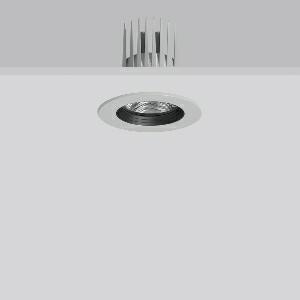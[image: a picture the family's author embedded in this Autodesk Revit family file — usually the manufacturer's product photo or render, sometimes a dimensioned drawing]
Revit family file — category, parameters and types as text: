
# Revit family: heledon_mini_e_901748_004_2_1676
name_source: partatom
category: Lighting Fixtures
units: mm (PartAtom-declared; Revit-internal decimal feet)

## family parameters
Cut with Voids When Loaded = No
Host = Face
Light Source = No
Part Type = Normal
Room Calculation Point = No
Round Connector Dimension = Use Diameter
Shared = No

## types (1)
- HELEDON mini E (1 x LED Modul 927, 3400 lm, 2700)
    Apparent Load = 29 VA
    Approval mark = CE
    CIE Flux Codes = 100 100 100 100 100
    Color Rendering = 92
    Color Temperature = 2700
    Default Elevation = 1800 mm
    Description = Series: HELEDON mini
Round recessed downlight. Housing: die-cast aluminium, powder-coated. Black plastic ring and recessed LED to prevent glare from the side. Optical assembly with reflector made of MIRO-Silver with 98% total light reflection for outstanding efficiency - can be changed without tools. Best colour rendering index Ra>90. Suitable for Recessed ceiling mounting. Installation without tools thanks to spring fastening system. Including separate LED converter with connecting cable 600 mm.High quality converter without flickering and stroboscopic effect. Through-wiring box (5 pole) available as accessory. The following accessories can be mounted without use of tools: interchangeable lenses, decorative glasses, honeycomb louvre, clear and frosted diffusers, white interchangeable plastic ring. 
Colour: silver
Diameter: 124 mm
Height: 3 mm
Cut-out diameter: 114 mm
Recess height: 170 mm
Luminaire: recess height: 120 mm
Lamp: LED
Socket: without socket
Colour temperature: 2700K
Colour rendering index (CRI): 92
System power: 29 W
Rated luminous flux: 3400 lm
Luminous efficiency: 117 lm/W
Control gear: Regulated power supply
Protection class: II
Type of protection: IP 20
    Height = 0 mm  [stored 0 ft]
    Lamp = 1 x LED Modul 927
    Lamp Light Flux = 3400 lm
    Lamp count = 1
    Length = 124 mm  [stored 0.406824 ft]
    Lifetime = 50000 h
    Luminous efficacy = 117 lm/W
    Manufacturer = RZB
    ModVariant = No
    Model = 901748.004.2
    Mounting Place = Ceiling
    Mounting Type = Recessed
    Number of Poles = 1
    OnlyDefault = Yes
    Power Factor = 1
    Product Name = HELEDON mini E
    Product group = Recessed downlights
    ProductGroupID = 402
    Protection Class = Protection class II
    Protection Degree = IP 20
    RLX_Detail_Level = 1
    RLX_Emergency_Light_Flux = 0 lm
    RLX_Emergency_Type = 0
    RLX_Emergency_Type_DB = No
    RlxData = <blob elided: 128665 chars, md5=aa7f4a00>
    Socket = socket
    Standby Power = 0 W
    System Light Flux = 3400 lm
    System Power = 29 W
    Type Comments = Product without accessories
    Type Image = 901657.004.jpg
    URL = http://relux.com
    VarID = ---
    Voltage = 230 V
    Voltage Range = 220-240 V
    Weight = 0.00 kg
    Width = 0 mm  [stored 0 ft]

note: [stored X ft] marks values corroborated as IEEE doubles in the binary element streams (Revit-internal decimal feet)

## geometry (parser evidence)
native form markers: Blend x4, Sweep x12
no freeform markers — native parametric forms only
